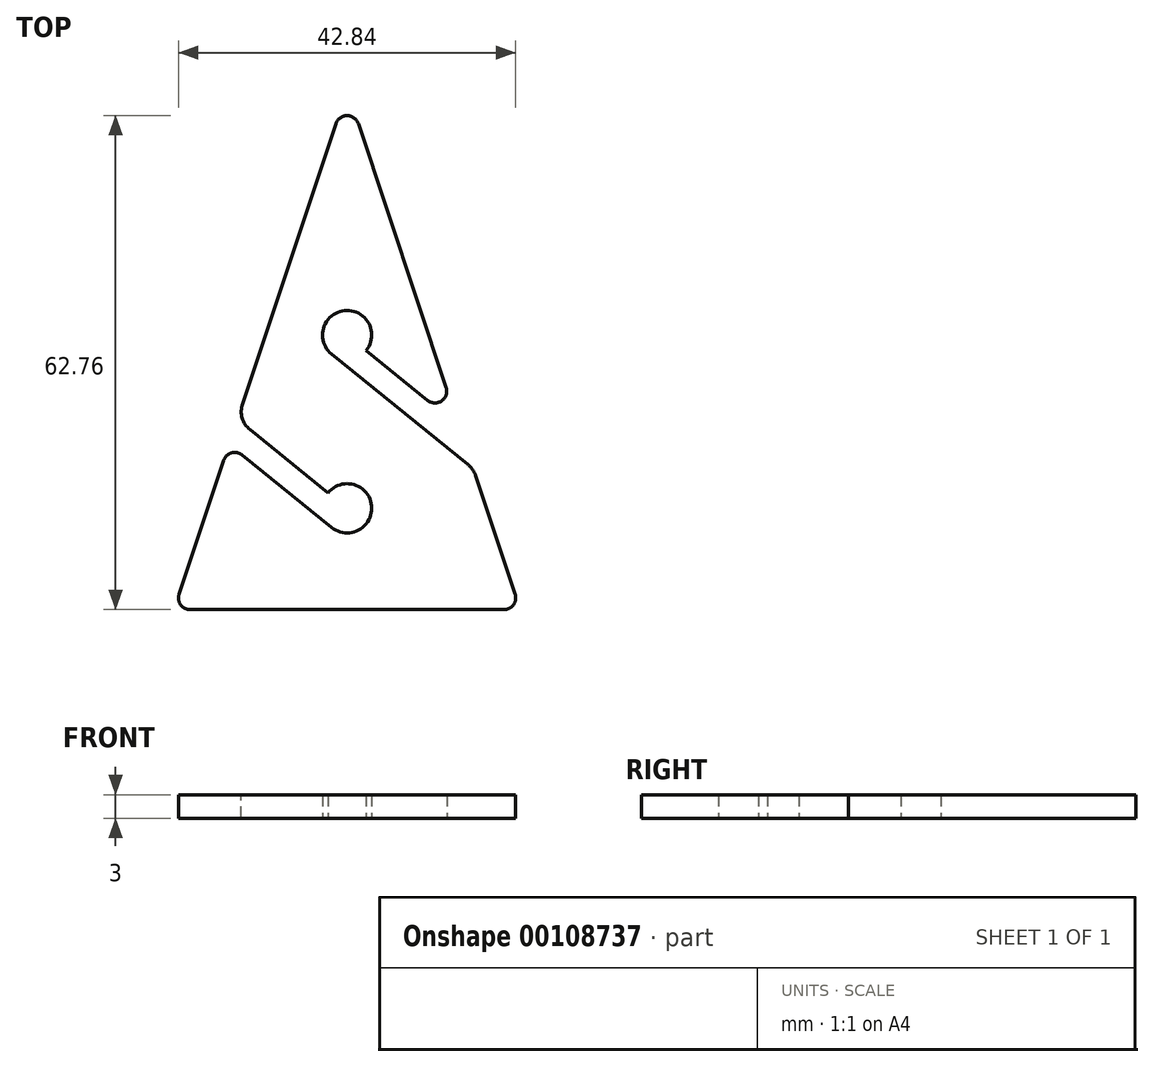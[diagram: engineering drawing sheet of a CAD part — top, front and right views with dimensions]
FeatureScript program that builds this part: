
annotation { "Feature Type Name" : "Feature", "Feature Type Description" : "" }
export const myFeature = defineFeature(function(context is Context, id is Id, definition is map)
    precondition{}
    {
        {
            var Q0;
            Q0=qCreatedBy(makeId("Top.planeOp"),FACE);
            var sketch = newSketch(context, id + "F0", { "sketchPlane" : qUnion([Q0])});
            skLineSegment(sketch, "E0", {"start": v(-22, 0) * mm, "end": v(22, 0) * mm});
            skLineSegment(sketch, "E1", {"start": v(22, 0) * mm, "end": v(0, 66) * mm});
            skLineSegment(sketch, "E2", {"start": v(0, 66) * mm, "end": v(-22, 0) * mm});
            skCircle(sketch, "E3", {"center": v(0, 12.88) * mm, "radius": 3.12 * mm});
            skCircle(sketch, "E4", {"center": v(0, 34.88) * mm, "radius": 3.12 * mm});
            skLineSegment(sketch, "E5", {"start": v(-1.97, 32.45) * mm, "end": v(16.05, 17.86) * mm});
            skLineSegment(sketch, "E6", {"start": v(0, 34.88) * mm, "end": v(14.21, 23.37) * mm});
            skLineSegment(sketch, "E7", {"start": v(-1.97, 10.45) * mm, "end": v(-15, 21) * mm});
            skLineSegment(sketch, "E8", {"start": v(0, 12.87) * mm, "end": v(-13.94, 24.17) * mm});
            skSolve(sketch);
        }
        {
            var Q0;
            {var subQ9=sQuery(id+"F0.wireOp",EDGE,"E0");Q0=makeQuery(id+"F0.imprint","IMPRINT",FACE,{"disambiguationData":[TD([[makeQuery(id+"F0.imprint","IMPRINT",EDGE,{"derivedFrom":subQ9}),1.0]])]});}
            extrude(context, id + "F1", {"entities" : qUnion([Q0]), "depth" : 3 * mm});
        }
        {
            var Q0;
            Q0=makeQuery(id+"F1.opExtrude","SWEPT_EDGE",EDGE,{"disambiguationData":[OSD([sQuery(id+"F0.wireOp",EDGE,"E0"),sQuery(id+"F0.wireOp",EDGE,"E2")])]});
            var Q1;
            Q1=makeQuery(id+"F1.opExtrude","SWEPT_EDGE",EDGE,{"disambiguationData":[OSD([sQuery(id+"F0.wireOp",EDGE,"E0"),sQuery(id+"F0.wireOp",EDGE,"E1")])]});
            var Q2;
            Q2=makeQuery(id+"F1.opExtrude","SWEPT_EDGE",EDGE,{"disambiguationData":[OSD([sQuery(id+"F0.wireOp",EDGE,"E1"),sQuery(id+"F0.wireOp",EDGE,"E6")])]});
            var Q3;
            Q3=makeQuery(id+"F1.opExtrude","SWEPT_EDGE",EDGE,{"disambiguationData":[OSD([sQuery(id+"F0.wireOp",EDGE,"E1"),sQuery(id+"F0.wireOp",EDGE,"E2")])]});
            var Q4;
            Q4=makeQuery(id+"F1.opExtrude","SWEPT_EDGE",EDGE,{"disambiguationData":[OSD([sQuery(id+"F0.wireOp",EDGE,"E2"),sQuery(id+"F0.wireOp",EDGE,"E7")])]});
            fillet(context, id + "F2", {"entities" : qUnion([Q0, Q1, Q2, Q3, Q4]), "radius" : 1.5 * mm, "tangentPropagation" : true, "allowEdgeOverflow" : false});
        }
        {
            var Q0;
            Q0=makeQuery(id+"F1.opExtrude","SWEPT_EDGE",EDGE,{"disambiguationData":[OSD([sQuery(id+"F0.wireOp",EDGE,"E2"),sQuery(id+"F0.wireOp",EDGE,"E8")])]});
            var Q1;
            Q1=makeQuery(id+"F1.opExtrude","SWEPT_EDGE",EDGE,{"disambiguationData":[OSD([sQuery(id+"F0.wireOp",EDGE,"E1"),sQuery(id+"F0.wireOp",EDGE,"E5")])]});
            fillet(context, id + "F3", {"entities" : qUnion([Q0, Q1]), "radius" : 3 * mm, "tangentPropagation" : true, "allowEdgeOverflow" : false});
        }
    });
